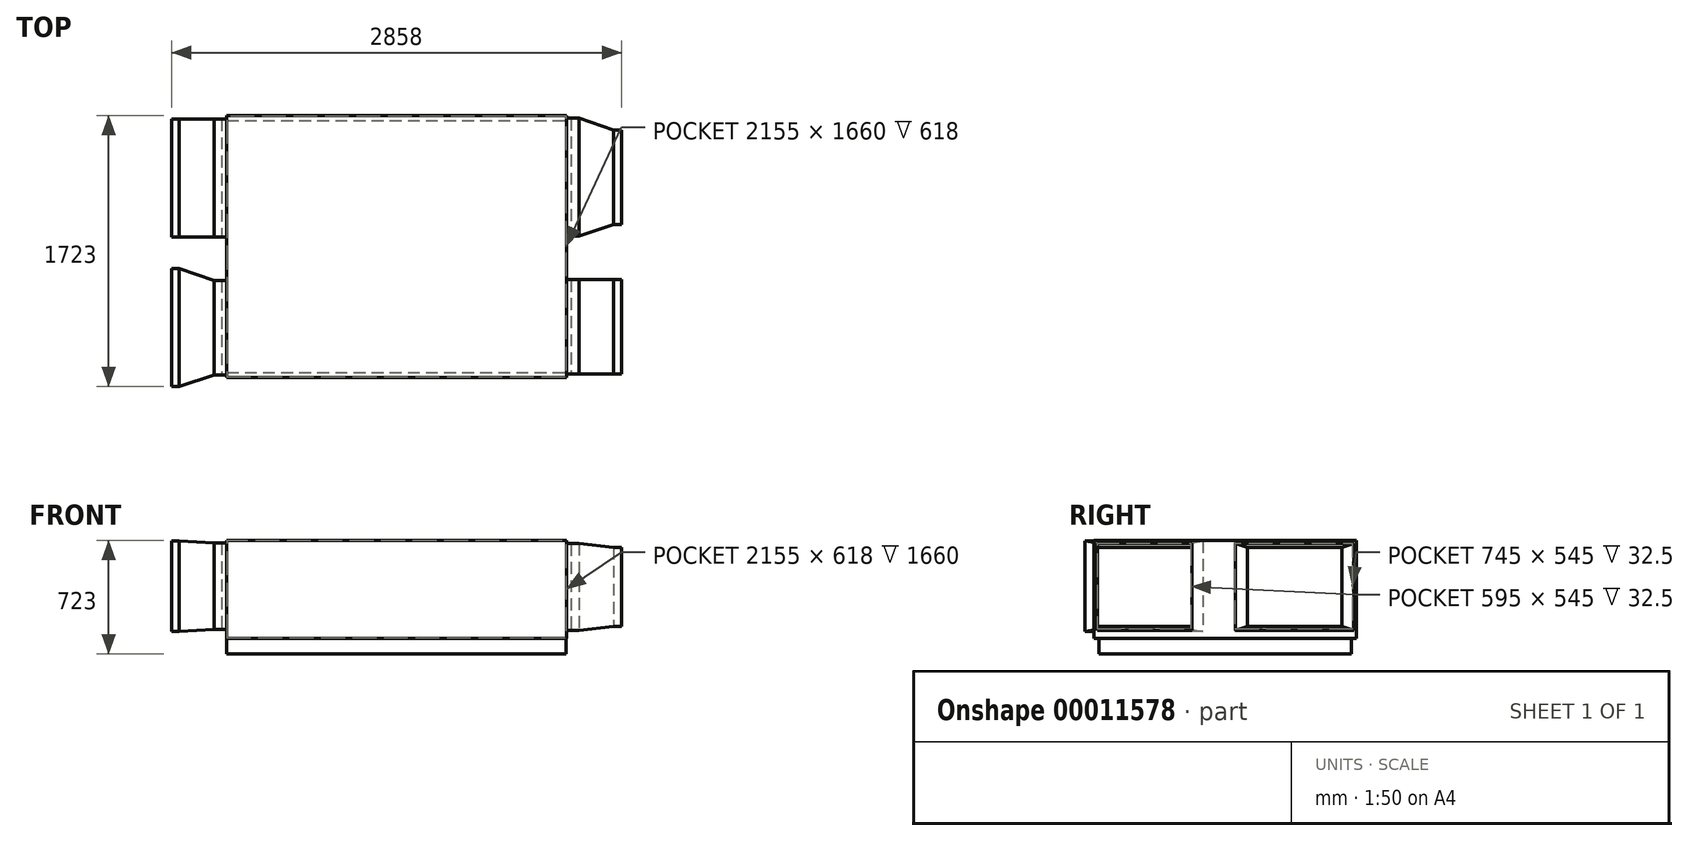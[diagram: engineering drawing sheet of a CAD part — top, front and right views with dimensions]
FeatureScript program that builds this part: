
annotation { "Feature Type Name" : "Feature", "Feature Type Description" : "" }
export const myFeature = defineFeature(function(context is Context, id is Id, definition is map)
    precondition{}
    {
        {
            var Q0;
            Q0=qCreatedBy(makeId("Top.planeOp"),FACE);
            var sketch = newSketch(context, id + "F0", { "sketchPlane" : qUnion([Q0])});
            skLineSegment(sketch, "E0.rect.bottom", {"start": v(-1080, -832.5) * mm, "end": v(1080, -832.5) * mm});
            skLineSegment(sketch, "E0.rect.top", {"start": v(-1080, 832.5) * mm, "end": v(1080, 832.5) * mm});
            skLineSegment(sketch, "E0.rect.left", {"start": v(-1080, -832.5) * mm, "end": v(-1080, 832.5) * mm});
            skLineSegment(sketch, "E0.rect.right", {"start": v(1080, -832.5) * mm, "end": v(1080, 832.5) * mm});
            skPoint(sketch, "E0.rect.middle", {"position": v(0, 0) * mm});
            skSolve(sketch);
        }
        {
            var Q0;
            Q0=makeQuery(id+"F0.imprint","IMPRINT",FACE,{"disambiguationData":[TD([[makeQuery(id+"F0.imprint","IMPRINT",EDGE,{"derivedFrom":sQuery(id+"F0.wireOp",EDGE,"E0.rect.bottom")}),1.0]])]});
            extrude(context, id + "F1", {"entities" : qUnion([Q0]), "depth" : 623 * mm});
        }
        {
            var Q0;
            Q0=qCreatedBy(makeId("Top.planeOp"),FACE);
            var sketch = newSketch(context, id + "F2", { "sketchPlane" : qUnion([Q0])});
            skLineSegment(sketch, "E1.rect.bottom", {"start": v(-1078, 801.5) * mm, "end": v(1078, 801.5) * mm});
            skLineSegment(sketch, "E1.rect.top", {"start": v(-1078, -801.5) * mm, "end": v(1078, -801.5) * mm});
            skLineSegment(sketch, "E1.rect.left", {"start": v(-1078, 801.5) * mm, "end": v(-1078, -801.5) * mm});
            skLineSegment(sketch, "E1.rect.right", {"start": v(1078, 801.5) * mm, "end": v(1078, -801.5) * mm});
            skPoint(sketch, "E1.rect.middle", {"position": v(0, 0) * mm});
            skSolve(sketch);
        }
        {
            var Q0;
            Q0=makeQuery(id+"F1.opExtrude","SWEPT_FACE",FACE,{"disambiguationData":[OSD([sQuery(id+"F0.wireOp",EDGE,"E0.rect.left")])]});
            var sketch = newSketch(context, id + "F3", { "sketchPlane" : qUnion([Q0])});
            skLineSegment(sketch, "E2.bottom", {"start": v(-810.5, 606) * mm, "end": v(-60.5, 606) * mm});
            skLineSegment(sketch, "E2.top", {"start": v(-810.5, 56) * mm, "end": v(-60.5, 56) * mm});
            skLineSegment(sketch, "E2.left", {"start": v(-810.5, 606) * mm, "end": v(-810.5, 56) * mm});
            skLineSegment(sketch, "E2.right", {"start": v(-60.5, 606) * mm, "end": v(-60.5, 56) * mm});
            skLineSegment(sketch, "E3.bottom", {"start": v(215.5, 606) * mm, "end": v(815.5, 606) * mm});
            skLineSegment(sketch, "E3.top", {"start": v(215.5, 56) * mm, "end": v(815.5, 56) * mm});
            skLineSegment(sketch, "E3.left", {"start": v(215.5, 606) * mm, "end": v(215.5, 56) * mm});
            skLineSegment(sketch, "E3.right", {"start": v(815.5, 606) * mm, "end": v(815.5, 56) * mm});
            skSolve(sketch);
        }
        {
            var Q0;
            Q0 = qSketchRegion(id + "F3", true);
            extrude(context, id + "F4", {"entities" : qUnion([Q0]), "operationType" : NewBodyOperationType.ADD, "depth" : 30 * mm});
        }
        {
            var Q0;
            Q0=makeQuery(id+"F1.opExtrude","SWEPT_FACE",FACE,{"disambiguationData":[OSD([sQuery(id+"F0.wireOp",EDGE,"E0.rect.right")])]});
            var sketch = newSketch(context, id + "F5", { "sketchPlane" : qUnion([Q0])});
            skLineSegment(sketch, "E4.left", {"start": v(-210.5, 601) * mm, "end": v(-210.5, 51) * mm});
            skLineSegment(sketch, "E5.0.MirrorCS", {"start": v(-210.5, 51) * mm, "end": v(-810.5, 51) * mm});
            skLineSegment(sketch, "E5.1.MirrorCS", {"start": v(-210.5, 601) * mm, "end": v(-810.5, 601) * mm});
            skLineSegment(sketch, "E5.2.MirrorCS", {"start": v(65.5, 601) * mm, "end": v(65.5, 51) * mm});
            skLineSegment(sketch, "E5.3.MirrorCS", {"start": v(815.5, 601) * mm, "end": v(815.5, 51) * mm});
            skLineSegment(sketch, "E5.4.MirrorCS", {"start": v(-810.5, 601) * mm, "end": v(-810.5, 51) * mm});
            skLineSegment(sketch, "E5.5.MirrorCS", {"start": v(815.5, 601) * mm, "end": v(65.5, 601) * mm});
            skLineSegment(sketch, "E5.6.MirrorCS", {"start": v(815.5, 51) * mm, "end": v(65.5, 51) * mm});
            skSolve(sketch);
        }
        {
            var Q0;
            Q0 = qSketchRegion(id + "F5", true);
            extrude(context, id + "F6", {"entities" : qUnion([Q0]), "operationType" : NewBodyOperationType.ADD, "depth" : 30 * mm});
        }
        {
            var Q0;
            Q0=makeQuery(id+"F4.opExtrude","CAP_FACE",FACE,{"disambiguationData":[OSD([sQuery(id+"F3.wireOp",EDGE,"E2.bottom"),sQuery(id+"F3.wireOp",EDGE,"E2.top"),sQuery(id+"F3.wireOp",EDGE,"E2.left"),sQuery(id+"F3.wireOp",EDGE,"E2.right")])],"isStart":false});
            var Q1;
            Q1=makeQuery(id+"F4.opExtrude","CAP_FACE",FACE,{"disambiguationData":[OSD([sQuery(id+"F3.wireOp",EDGE,"E3.bottom"),sQuery(id+"F3.wireOp",EDGE,"E3.top"),sQuery(id+"F3.wireOp",EDGE,"E3.left"),sQuery(id+"F3.wireOp",EDGE,"E3.right")])],"isStart":false});
            var Q2;
            Q2=makeQuery(id+"F6.opExtrude","CAP_FACE",FACE,{"disambiguationData":[OSD([sQuery(id+"F5.wireOp",EDGE,"E4.left"),sQuery(id+"F5.wireOp",EDGE,"E5.0.MirrorCS"),sQuery(id+"F5.wireOp",EDGE,"E5.1.MirrorCS"),sQuery(id+"F5.wireOp",EDGE,"E5.4.MirrorCS")])],"isStart":false});
            var Q3;
            Q3=makeQuery(id+"F6.opExtrude","CAP_FACE",FACE,{"disambiguationData":[OSD([sQuery(id+"F5.wireOp",EDGE,"E5.2.MirrorCS"),sQuery(id+"F5.wireOp",EDGE,"E5.3.MirrorCS"),sQuery(id+"F5.wireOp",EDGE,"E5.5.MirrorCS"),sQuery(id+"F5.wireOp",EDGE,"E5.6.MirrorCS")])],"isStart":false});
            shell(context, id + "F7", {"entities" : qUnion([Q0, Q1, Q2, Q3]), "thickness" : 2.5 * mm});
        }
        {
            var Q0;
            Q0 = qSketchRegion(id + "F2", true);
            extrude(context, id + "F8", {"entities" : qUnion([Q0]), "operationType" : NewBodyOperationType.ADD, "oppositeDirection" : true, "depth" : 100 * mm});
        }
        {
            var Q0;
            Q0=makeQuery(id+"F4.opExtrude","CAP_FACE",FACE,{"disambiguationData":[OSD([sQuery(id+"F3.wireOp",EDGE,"E2.bottom"),sQuery(id+"F3.wireOp",EDGE,"E2.top"),sQuery(id+"F3.wireOp",EDGE,"E2.left"),sQuery(id+"F3.wireOp",EDGE,"E2.right")])],"isStart":false});
            var sketch = newSketch(context, id + "F9", { "sketchPlane" : qUnion([Q0])});
            skLineSegment(sketch, "E6.bottom", {"start": v(-810.5, 606) * mm, "end": v(-60.5, 606) * mm});
            skLineSegment(sketch, "E6.top", {"start": v(-810.5, 56) * mm, "end": v(-60.5, 56) * mm});
            skLineSegment(sketch, "E6.left", {"start": v(-810.5, 606) * mm, "end": v(-810.5, 56) * mm});
            skLineSegment(sketch, "E6.right", {"start": v(-60.5, 606) * mm, "end": v(-60.5, 56) * mm});
            skSolve(sketch);
        }
        {
            var Q0;
            Q0 = qSketchRegion(id + "F9", true);
            extrude(context, id + "F10", {"entities" : qUnion([Q0]), "operationType" : NewBodyOperationType.ADD, "depth" : 50 * mm});
        }
        {
            var Q0;
            Q0=makeQuery(id+"F10.opExtrude","CAP_FACE",FACE,{"disambiguationData":[OSD([sQuery(id+"F9.wireOp",EDGE,"E6.bottom"),sQuery(id+"F9.wireOp",EDGE,"E6.top"),sQuery(id+"F9.wireOp",EDGE,"E6.left"),sQuery(id+"F9.wireOp",EDGE,"E6.right")])],"isStart":false});
            cPlane(context, id + "F11", {"entities" : qUnion([Q0]), "cplaneType" : CPlaneType.OFFSET, "offset" : 219 * mm, "width" : 150 * mm, "height" : 150 * mm});
        }
        {
            var Q0;
            Q0=qCreatedBy(id+"F11.planeOp",FACE);
            var sketch = newSketch(context, id + "F12", { "sketchPlane" : qUnion([Q0])});
            skLineSegment(sketch, "E7.rect.bottom", {"start": v(-810.5, 618.5) * mm, "end": v(-60.5, 618.5) * mm});
            skLineSegment(sketch, "E7.rect.top", {"start": v(-810.5, 43.5) * mm, "end": v(-60.5, 43.5) * mm});
            skLineSegment(sketch, "E7.rect.left", {"start": v(-810.5, 618.5) * mm, "end": v(-810.5, 43.5) * mm});
            skLineSegment(sketch, "E7.rect.right", {"start": v(-60.5, 618.5) * mm, "end": v(-60.5, 43.5) * mm});
            skPoint(sketch, "E7.rect.middle", {"position": v(-435.5, 331) * mm});
            skSolve(sketch);
        }
        {
            var Q1;
            Q1=makeQuery(id+"F10.opExtrude","CAP_FACE",FACE,{"disambiguationData":[OSD([sQuery(id+"F9.wireOp",EDGE,"E6.bottom"),sQuery(id+"F9.wireOp",EDGE,"E6.top"),sQuery(id+"F9.wireOp",EDGE,"E6.left"),sQuery(id+"F9.wireOp",EDGE,"E6.right")])],"isStart":false});
            var Q2;
            Q2=makeQuery(id+"F12.imprint","IMPRINT",FACE,{"disambiguationData":[TD([[makeQuery(id+"F12.imprint","IMPRINT",EDGE,{"derivedFrom":sQuery(id+"F12.wireOp",EDGE,"E7.rect.bottom")}),-1.0]])]});
            loft(context, id + "F13", {"operationType" : NewBodyOperationType.ADD, "sheetProfilesArray" : [{ "sheetProfileEntities" : qUnion([Q1]) }, { "sheetProfileEntities" : qUnion([Q2]) }]});
        }
        {
            var Q0;
            Q0=makeQuery(id+"F13.opLoft","CAP_FACE",FACE,{"disambiguationData":[OSD([makeQuery(id+"F12.imprint","IMPRINT",FACE,{"disambiguationData":[TD([[makeQuery(id+"F12.imprint","IMPRINT",EDGE,{"derivedFrom":sQuery(id+"F12.wireOp",EDGE,"E7.rect.bottom")}),-1.0]])]})])],"isStart":true});
            extrude(context, id + "F14", {"entities" : qUnion([Q0]), "operationType" : NewBodyOperationType.ADD, "depth" : 50 * mm});
        }
        {
            var Q0;
            Q0=makeQuery(id+"F4.opExtrude","CAP_FACE",FACE,{"disambiguationData":[OSD([sQuery(id+"F3.wireOp",EDGE,"E3.bottom"),sQuery(id+"F3.wireOp",EDGE,"E3.top"),sQuery(id+"F3.wireOp",EDGE,"E3.left"),sQuery(id+"F3.wireOp",EDGE,"E3.right")])],"isStart":false});
            var sketch = newSketch(context, id + "F15", { "sketchPlane" : qUnion([Q0])});
            skLineSegment(sketch, "E8.bottom", {"start": v(215.5, 606) * mm, "end": v(815.5, 606) * mm});
            skLineSegment(sketch, "E8.top", {"start": v(215.5, 56) * mm, "end": v(815.5, 56) * mm});
            skLineSegment(sketch, "E8.left", {"start": v(215.5, 606) * mm, "end": v(215.5, 56) * mm});
            skLineSegment(sketch, "E8.right", {"start": v(815.5, 606) * mm, "end": v(815.5, 56) * mm});
            skSolve(sketch);
        }
        {
            var Q0;
            Q0 = qSketchRegion(id + "F15", true);
            extrude(context, id + "F16", {"entities" : qUnion([Q0]), "operationType" : NewBodyOperationType.ADD, "depth" : 50 * mm});
        }
        {
            var Q0;
            Q0=qCreatedBy(id+"F11.planeOp",FACE);
            var sketch = newSketch(context, id + "F17", { "sketchPlane" : qUnion([Q0])});
            skLineSegment(sketch, "E9.rect.bottom", {"start": v(140.5, 618.5) * mm, "end": v(890.5, 618.5) * mm});
            skLineSegment(sketch, "E9.rect.top", {"start": v(140.5, 43.5) * mm, "end": v(890.5, 43.5) * mm});
            skLineSegment(sketch, "E9.rect.left", {"start": v(140.5, 618.5) * mm, "end": v(140.5, 43.5) * mm});
            skLineSegment(sketch, "E9.rect.right", {"start": v(890.5, 618.5) * mm, "end": v(890.5, 43.5) * mm});
            skPoint(sketch, "E9.rect.middle", {"position": v(515.5, 331) * mm});
            skSolve(sketch);
        }
        {
            var Q1;
            Q1=makeQuery(id+"F16.opExtrude","CAP_FACE",FACE,{"disambiguationData":[OSD([sQuery(id+"F15.wireOp",EDGE,"E8.bottom"),sQuery(id+"F15.wireOp",EDGE,"E8.top"),sQuery(id+"F15.wireOp",EDGE,"E8.left"),sQuery(id+"F15.wireOp",EDGE,"E8.right")])],"isStart":false});
            var Q2;
            Q2=makeQuery(id+"F17.imprint","IMPRINT",FACE,{"disambiguationData":[TD([[makeQuery(id+"F17.imprint","IMPRINT",EDGE,{"derivedFrom":sQuery(id+"F17.wireOp",EDGE,"E9.rect.bottom")}),-1.0]])]});
            loft(context, id + "F18", {"operationType" : NewBodyOperationType.ADD, "sheetProfilesArray" : [{ "sheetProfileEntities" : qUnion([Q1]) }, { "sheetProfileEntities" : qUnion([Q2]) }]});
        }
        {
            var Q0;
            Q0=makeQuery(id+"F18.opLoft","CAP_FACE",FACE,{"disambiguationData":[OSD([makeQuery(id+"F17.imprint","IMPRINT",FACE,{"disambiguationData":[TD([[makeQuery(id+"F17.imprint","IMPRINT",EDGE,{"derivedFrom":sQuery(id+"F17.wireOp",EDGE,"E9.rect.bottom")}),-1.0]])]})])],"isStart":true});
            extrude(context, id + "F19", {"entities" : qUnion([Q0]), "operationType" : NewBodyOperationType.ADD, "depth" : 50 * mm});
        }
        {
            var Q0;
            Q0=makeQuery(id+"F6.opExtrude","CAP_FACE",FACE,{"disambiguationData":[OSD([sQuery(id+"F5.wireOp",EDGE,"E4.left"),sQuery(id+"F5.wireOp",EDGE,"E5.0.MirrorCS"),sQuery(id+"F5.wireOp",EDGE,"E5.1.MirrorCS"),sQuery(id+"F5.wireOp",EDGE,"E5.4.MirrorCS")])],"isStart":false});
            var sketch = newSketch(context, id + "F20", { "sketchPlane" : qUnion([Q0])});
            skLineSegment(sketch, "E10.bottom", {"start": v(-810.5, 601) * mm, "end": v(-210.5, 601) * mm});
            skLineSegment(sketch, "E10.top", {"start": v(-810.5, 51) * mm, "end": v(-210.5, 51) * mm});
            skLineSegment(sketch, "E10.left", {"start": v(-810.5, 601) * mm, "end": v(-810.5, 51) * mm});
            skLineSegment(sketch, "E10.right", {"start": v(-210.5, 601) * mm, "end": v(-210.5, 51) * mm});
            skSolve(sketch);
        }
        {
            var Q0;
            Q0 = qSketchRegion(id + "F20", true);
            extrude(context, id + "F21", {"entities" : qUnion([Q0]), "operationType" : NewBodyOperationType.ADD, "depth" : 50 * mm});
        }
        {
            var Q0;
            Q0=makeQuery(id+"F6.opExtrude","CAP_FACE",FACE,{"disambiguationData":[OSD([sQuery(id+"F5.wireOp",EDGE,"E5.2.MirrorCS"),sQuery(id+"F5.wireOp",EDGE,"E5.3.MirrorCS"),sQuery(id+"F5.wireOp",EDGE,"E5.5.MirrorCS"),sQuery(id+"F5.wireOp",EDGE,"E5.6.MirrorCS")])],"isStart":false});
            var sketch = newSketch(context, id + "F22", { "sketchPlane" : qUnion([Q0])});
            skLineSegment(sketch, "E11.bottom", {"start": v(65.5, 601) * mm, "end": v(815.5, 601) * mm});
            skLineSegment(sketch, "E11.top", {"start": v(65.5, 51) * mm, "end": v(815.5, 51) * mm});
            skLineSegment(sketch, "E11.left", {"start": v(65.5, 601) * mm, "end": v(65.5, 51) * mm});
            skLineSegment(sketch, "E11.right", {"start": v(815.5, 601) * mm, "end": v(815.5, 51) * mm});
            skSolve(sketch);
        }
        {
            var Q0;
            Q0 = qSketchRegion(id + "F22", true);
            extrude(context, id + "F23", {"entities" : qUnion([Q0]), "operationType" : NewBodyOperationType.ADD, "depth" : 50 * mm});
        }
        {
            var Q0;
            Q0=makeQuery(id+"F21.opExtrude","CAP_FACE",FACE,{"disambiguationData":[OSD([sQuery(id+"F20.wireOp",EDGE,"E10.bottom"),sQuery(id+"F20.wireOp",EDGE,"E10.top"),sQuery(id+"F20.wireOp",EDGE,"E10.left"),sQuery(id+"F20.wireOp",EDGE,"E10.right")])],"isStart":false});
            cPlane(context, id + "F24", {"entities" : qUnion([Q0]), "cplaneType" : CPlaneType.OFFSET, "offset" : 219 * mm, "width" : 150 * mm, "height" : 150 * mm});
        }
        {
            var Q0;
            Q0=qCreatedBy(id+"F24.planeOp",FACE);
            var sketch = newSketch(context, id + "F25", { "sketchPlane" : qUnion([Q0])});
            skLineSegment(sketch, "E12.rect.bottom", {"start": v(-810.5, 576) * mm, "end": v(-210.5, 576) * mm});
            skLineSegment(sketch, "E12.rect.top", {"start": v(-810.5, 76) * mm, "end": v(-210.5, 76) * mm});
            skLineSegment(sketch, "E12.rect.left", {"start": v(-810.5, 576) * mm, "end": v(-810.5, 76) * mm});
            skLineSegment(sketch, "E12.rect.right", {"start": v(-210.5, 576) * mm, "end": v(-210.5, 76) * mm});
            skPoint(sketch, "E12.rect.middle", {"position": v(-510.5, 326) * mm});
            skSolve(sketch);
        }
        {
            var Q1;
            Q1=makeQuery(id+"F21.opExtrude","CAP_FACE",FACE,{"disambiguationData":[OSD([sQuery(id+"F20.wireOp",EDGE,"E10.bottom"),sQuery(id+"F20.wireOp",EDGE,"E10.top"),sQuery(id+"F20.wireOp",EDGE,"E10.left"),sQuery(id+"F20.wireOp",EDGE,"E10.right")])],"isStart":false});
            var Q2;
            Q2=makeQuery(id+"F25.imprint","IMPRINT",FACE,{"disambiguationData":[TD([[makeQuery(id+"F25.imprint","IMPRINT",EDGE,{"derivedFrom":sQuery(id+"F25.wireOp",EDGE,"E12.rect.bottom")}),-1.0]])]});
            loft(context, id + "F26", {"operationType" : NewBodyOperationType.ADD, "sheetProfilesArray" : [{ "sheetProfileEntities" : qUnion([Q1]) }, { "sheetProfileEntities" : qUnion([Q2]) }]});
        }
        {
            var Q0;
            Q0=makeQuery(id+"F26.opLoft","CAP_FACE",FACE,{"disambiguationData":[OSD([makeQuery(id+"F25.imprint","IMPRINT",FACE,{"disambiguationData":[TD([[makeQuery(id+"F25.imprint","IMPRINT",EDGE,{"derivedFrom":sQuery(id+"F25.wireOp",EDGE,"E12.rect.bottom")}),-1.0]])]})])],"isStart":true});
            extrude(context, id + "F27", {"entities" : qUnion([Q0]), "operationType" : NewBodyOperationType.ADD, "depth" : 50 * mm});
        }
        {
            var Q0;
            Q0=qCreatedBy(id+"F24.planeOp",FACE);
            var sketch = newSketch(context, id + "F28", { "sketchPlane" : qUnion([Q0])});
            skLineSegment(sketch, "E13.rect.bottom", {"start": v(140.5, 576) * mm, "end": v(740.5, 576) * mm});
            skLineSegment(sketch, "E13.rect.top", {"start": v(140.5, 76) * mm, "end": v(740.5, 76) * mm});
            skLineSegment(sketch, "E13.rect.left", {"start": v(140.5, 576) * mm, "end": v(140.5, 76) * mm});
            skLineSegment(sketch, "E13.rect.right", {"start": v(740.5, 576) * mm, "end": v(740.5, 76) * mm});
            skPoint(sketch, "E13.rect.middle", {"position": v(440.5, 326) * mm});
            skSolve(sketch);
        }
        {
            var Q1;
            Q1=makeQuery(id+"F23.opExtrude","CAP_FACE",FACE,{"disambiguationData":[OSD([sQuery(id+"F22.wireOp",EDGE,"E11.bottom"),sQuery(id+"F22.wireOp",EDGE,"E11.top"),sQuery(id+"F22.wireOp",EDGE,"E11.left"),sQuery(id+"F22.wireOp",EDGE,"E11.right")])],"isStart":false});
            var Q2;
            Q2=makeQuery(id+"F28.imprint","IMPRINT",FACE,{"disambiguationData":[TD([[makeQuery(id+"F28.imprint","IMPRINT",EDGE,{"derivedFrom":sQuery(id+"F28.wireOp",EDGE,"E13.rect.bottom")}),-1.0]])]});
            loft(context, id + "F29", {"operationType" : NewBodyOperationType.ADD, "sheetProfilesArray" : [{ "sheetProfileEntities" : qUnion([Q1]) }, { "sheetProfileEntities" : qUnion([Q2]) }]});
        }
        {
            var Q0;
            Q0=makeQuery(id+"F29.opLoft","CAP_FACE",FACE,{"disambiguationData":[OSD([makeQuery(id+"F28.imprint","IMPRINT",FACE,{"disambiguationData":[TD([[makeQuery(id+"F28.imprint","IMPRINT",EDGE,{"derivedFrom":sQuery(id+"F28.wireOp",EDGE,"E13.rect.bottom")}),-1.0]])]})])],"isStart":true});
            extrude(context, id + "F30", {"entities" : qUnion([Q0]), "operationType" : NewBodyOperationType.ADD, "depth" : 50 * mm});
        }
    });
